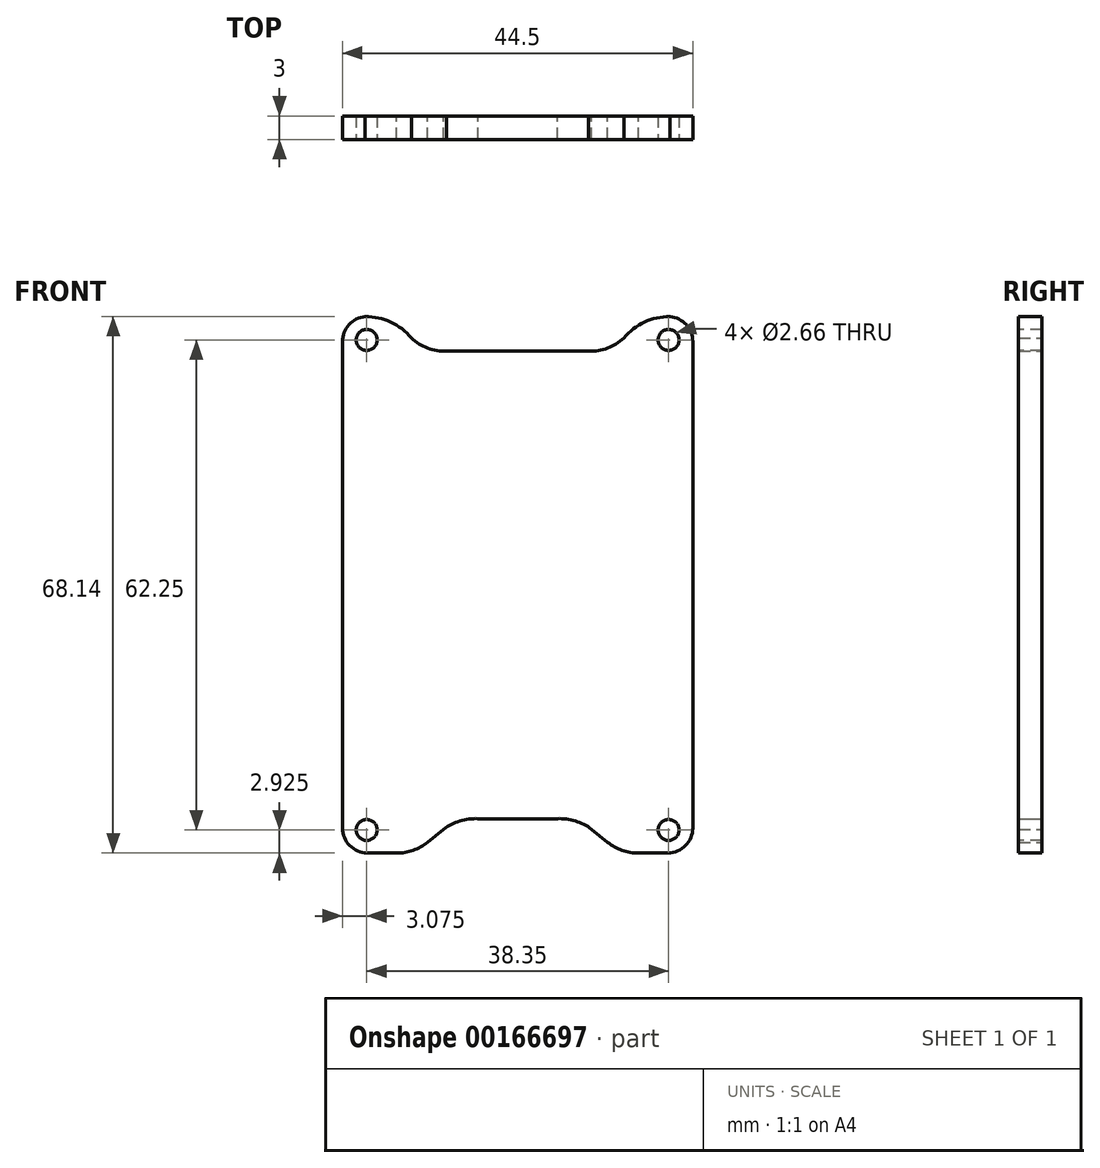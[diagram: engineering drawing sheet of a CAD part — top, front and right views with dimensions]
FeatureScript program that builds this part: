
annotation { "Feature Type Name" : "Feature", "Feature Type Description" : "" }
export const myFeature = defineFeature(function(context is Context, id is Id, definition is map)
    precondition{}
    {
        {
            var Q0;
            Q0=qCreatedBy(makeId("Front.planeOp"),FACE);
            var sketch = newSketch(context, id + "F0", { "sketchPlane" : qUnion([Q0])});
            skLineSegment(sketch, "E0", {"start": v(-22.25, 30.9) * mm, "end": v(-22.25, -30.86) * mm});
            skArc(sketch, "E1", {"start": v(-19.36, 34.09) * mm, "mid": v(-21.42, 33.05) * mm, "end": v(-22.25, 30.9) * mm});
            skArc(sketch, "E2", {"start": v(-13.5, 31.38) * mm, "mid": v(-16.12, 33.4) * mm, "end": v(-19.36, 34.09) * mm});
            skArc(sketch, "E3", {"start": v(-13.5, 31.38) * mm, "mid": v(-11.43, 30.08) * mm, "end": v(-9.03, 29.7) * mm});
            skLineSegment(sketch, "E4", {"start": v(-9.03, 29.7) * mm, "end": v(0, 29.7) * mm});
            skArc(sketch, "E5", {"start": v(-22.25, -30.86) * mm, "mid": v(-21.33, -33.1) * mm, "end": v(-19.1, -34.04) * mm});
            skArc(sketch, "E6", {"start": v(-15.37, -34.04) * mm, "mid": v(-13.28, -33.72) * mm, "end": v(-11.44, -32.68) * mm});
            skArc(sketch, "E7", {"start": v(-5.04, -29.7) * mm, "mid": v(-7.33, -29.98) * mm, "end": v(-9.39, -31.04) * mm});
            skLineSegment(sketch, "E8", {"start": v(-19.1, -34.04) * mm, "end": v(-15.37, -34.04) * mm});
            skLineSegment(sketch, "E9", {"start": v(-11.44, -32.68) * mm, "end": v(-9.39, -31.04) * mm});
            skLineSegment(sketch, "E10", {"start": v(-5.04, -29.7) * mm, "end": v(0, -29.7) * mm});
            skArc(sketch, "E11.MirrorCS", {"start": v(5.04, -29.7) * mm, "mid": v(7.33, -29.98) * mm, "end": v(9.39, -31.04) * mm});
            skArc(sketch, "E12.MirrorCS", {"start": v(19.36, 34.09) * mm, "mid": v(21.42, 33.05) * mm, "end": v(22.25, 30.9) * mm});
            skArc(sketch, "E13.MirrorCS", {"start": v(13.5, 31.38) * mm, "mid": v(16.12, 33.4) * mm, "end": v(19.36, 34.09) * mm});
            skArc(sketch, "E14.MirrorCS", {"start": v(13.5, 31.38) * mm, "mid": v(11.43, 30.08) * mm, "end": v(9.03, 29.7) * mm});
            skLineSegment(sketch, "E15.MirrorCS", {"start": v(11.44, -32.68) * mm, "end": v(9.39, -31.04) * mm});
            skArc(sketch, "E16.MirrorCS", {"start": v(22.25, -30.86) * mm, "mid": v(21.33, -33.1) * mm, "end": v(19.1, -34.04) * mm});
            skArc(sketch, "E17.MirrorCS", {"start": v(15.37, -34.04) * mm, "mid": v(13.28, -33.72) * mm, "end": v(11.44, -32.68) * mm});
            skLineSegment(sketch, "E18.MirrorCS", {"start": v(19.1, -34.04) * mm, "end": v(15.37, -34.04) * mm});
            skLineSegment(sketch, "E19.MirrorCS", {"start": v(5.04, -29.7) * mm, "end": v(0, -29.7) * mm});
            skLineSegment(sketch, "E20.MirrorCS", {"start": v(22.25, 30.9) * mm, "end": v(22.25, -30.86) * mm});
            skLineSegment(sketch, "E21.MirrorCS", {"start": v(9.03, 29.7) * mm, "end": v(0, 29.7) * mm});
            skLineSegment(sketch, "E22", {"start": v(-19.04, 30.9) * mm, "end": v(19.04, 30.9) * mm, "construction": true});
            skLineSegment(sketch, "E23", {"start": v(-19.26, 26.6) * mm, "end": v(19.26, 26.6) * mm, "construction": true});
            skLineSegment(sketch, "E24", {"start": v(-9.29, 35.78) * mm, "end": v(9.29, 35.78) * mm, "construction": true});
            skLineSegment(sketch, "E25", {"start": v(-15.2, -28.18) * mm, "end": v(15.2, -28.18) * mm, "construction": true});
            skLineSegment(sketch, "E26", {"start": v(-19.07, -30.86) * mm, "end": v(19.07, -30.86) * mm, "construction": true});
            skLineSegment(sketch, "E27", {"start": v(-5.4, -36.28) * mm, "end": v(5.4, -36.28) * mm, "construction": true});
            skSolve(sketch);
        }
        {
            var Q0;
            Q0=qSketchRegion(id+"F0",true);
            extrude(context, id + "F1", {"entities" : qUnion([Q0]), "depth" : 3 * mm});
        }
        {
            var Q0;
            Q0=makeQuery(id+"F1.opExtrude","CAP_FACE",FACE,{"disambiguationData":[OSD([sQuery(id+"F0.wireOp",EDGE,"E0"),sQuery(id+"F0.wireOp",EDGE,"E1"),sQuery(id+"F0.wireOp",EDGE,"E2"),sQuery(id+"F0.wireOp",EDGE,"E3"),sQuery(id+"F0.wireOp",EDGE,"E4"),sQuery(id+"F0.wireOp",EDGE,"E5"),sQuery(id+"F0.wireOp",EDGE,"E6"),sQuery(id+"F0.wireOp",EDGE,"E7"),sQuery(id+"F0.wireOp",EDGE,"E8"),sQuery(id+"F0.wireOp",EDGE,"E9"),sQuery(id+"F0.wireOp",EDGE,"E10"),sQuery(id+"F0.wireOp",EDGE,"E11.MirrorCS"),sQuery(id+"F0.wireOp",EDGE,"E12.MirrorCS"),sQuery(id+"F0.wireOp",EDGE,"E13.MirrorCS"),sQuery(id+"F0.wireOp",EDGE,"E14.MirrorCS"),sQuery(id+"F0.wireOp",EDGE,"E15.MirrorCS"),sQuery(id+"F0.wireOp",EDGE,"E16.MirrorCS"),sQuery(id+"F0.wireOp",EDGE,"E17.MirrorCS"),sQuery(id+"F0.wireOp",EDGE,"E18.MirrorCS"),sQuery(id+"F0.wireOp",EDGE,"E19.MirrorCS"),sQuery(id+"F0.wireOp",EDGE,"E20.MirrorCS"),sQuery(id+"F0.wireOp",EDGE,"E21.MirrorCS")])],"isStart":false});
            var sketch = newSketch(context, id + "F2", { "sketchPlane" : qUnion([Q0])});
            skCircle(sketch, "E28", {"center": v(-19.17, 31.12) * mm, "radius": 1.33 * mm});
            skCircle(sketch, "E29", {"center": v(19.17, 31.12) * mm, "radius": 1.33 * mm});
            skCircle(sketch, "E30", {"center": v(19.17, -31.12) * mm, "radius": 1.33 * mm});
            skCircle(sketch, "E31", {"center": v(-19.17, -31.12) * mm, "radius": 1.33 * mm});
            skLineSegment(sketch, "E32", {"start": v(-19.17, 31.12) * mm, "end": v(19.17, 31.12) * mm, "construction": true});
            skLineSegment(sketch, "E33", {"start": v(-19.17, -31.12) * mm, "end": v(19.17, -31.12) * mm, "construction": true});
            skLineSegment(sketch, "E34", {"start": v(19.17, -31.12) * mm, "end": v(19.17, 31.12) * mm, "construction": true});
            skLineSegment(sketch, "E35", {"start": v(-19.17, 31.12) * mm, "end": v(-19.17, -31.12) * mm, "construction": true});
            skSolve(sketch);
        }
        {
            var Q0;
            Q0=qSketchRegion(id+"F2",true);
            extrude(context, id + "F3", {"entities" : qUnion([Q0]), "operationType" : NewBodyOperationType.REMOVE, "endBound" : BoundingType.THROUGH_ALL, "oppositeDirection" : true, "depth" : 25 * mm});
        }
    });
